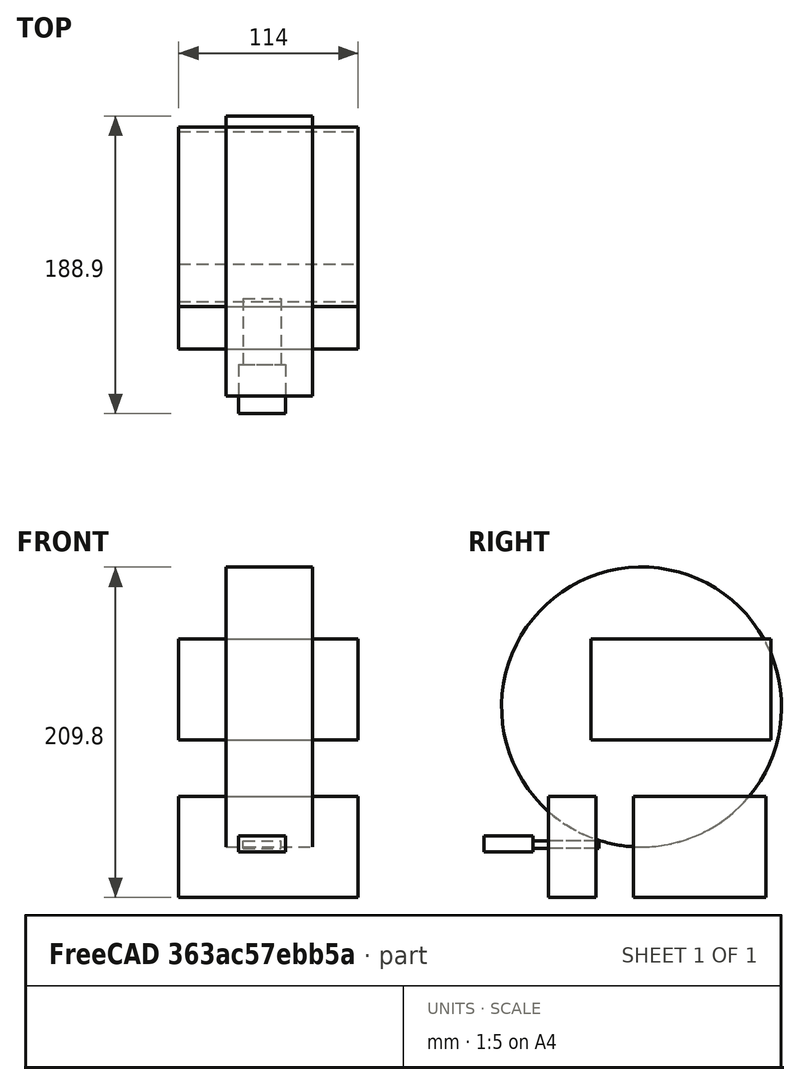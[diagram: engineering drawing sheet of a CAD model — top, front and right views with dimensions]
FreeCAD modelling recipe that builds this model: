
FCSTD DOCUMENT  (FreeCAD 0.18R16033 (Git))
Label: blocks
License: All rights reserved
LicenseURL: http://en.wikipedia.org/wiki/All_rights_reserved
objects: Part::Box×5, Part::MultiFuse×1, Part::Cylinder×1
note: 7 computed .brp shape members not serialized (recipe doc carries the construction recipe); baked Part::Feature solids carry a one-line shape summary decoded from their .brp

FEATURE [Part::Box] Box  label="Top"
  AttacherType = Attacher::AttachEngine3D
  Height = 64
  Length = 114
  Placement = pos=(0,27,0) rot=(0,0,1;0rad)
  Width = 84
  expr: Width = 114 - 30
FEATURE [Part::Box] Box001  label="Bottom"
  AttacherType = Attacher::AttachEngine3D
  Height = 64
  Length = 114
  Placement = pos=(0,0,100) rot=(0,0,1;0rad)
  Width = 114
FEATURE [Part::Box] Box002  label="Cube"
  AttacherType = Attacher::AttachEngine3D
  Height = 10
  Length = 31
  Width = 30
FEATURE [Part::Box] Box003  label="Cube001"
  AttacherType = Attacher::AttachEngine3D
  Height = 5
  Length = 42
  Placement = pos=(-42,3,2) rot=(0,0,1;0rad)
  Width = 24
FEATURE [Part::MultiFuse] Fusion
  Placement = pos=(38,-37,29) rot=(0,0,1;4.71239rad)
  Shapes = -> [Box002,Box003]
FEATURE [Part::Cylinder] Cylinder
  Angle = 360
  AttacherType = Attacher::AttachEngine3D
  Height = 55
  Placement = pos=(30,32,120.9) rot=(0,1,0;1.5708rad)
  Radius = 88.9
  expr: Placement.Base.z = 88.90000000000001 + 64 - 32
FEATURE [Part::Box] Box004  label="Top001"
  AttacherType = Attacher::AttachEngine3D
  Height = 64
  Length = 114
  Placement = pos=(0,-27,0) rot=(0,0,1;0rad)
  Width = 30
  expr: Width = 30
